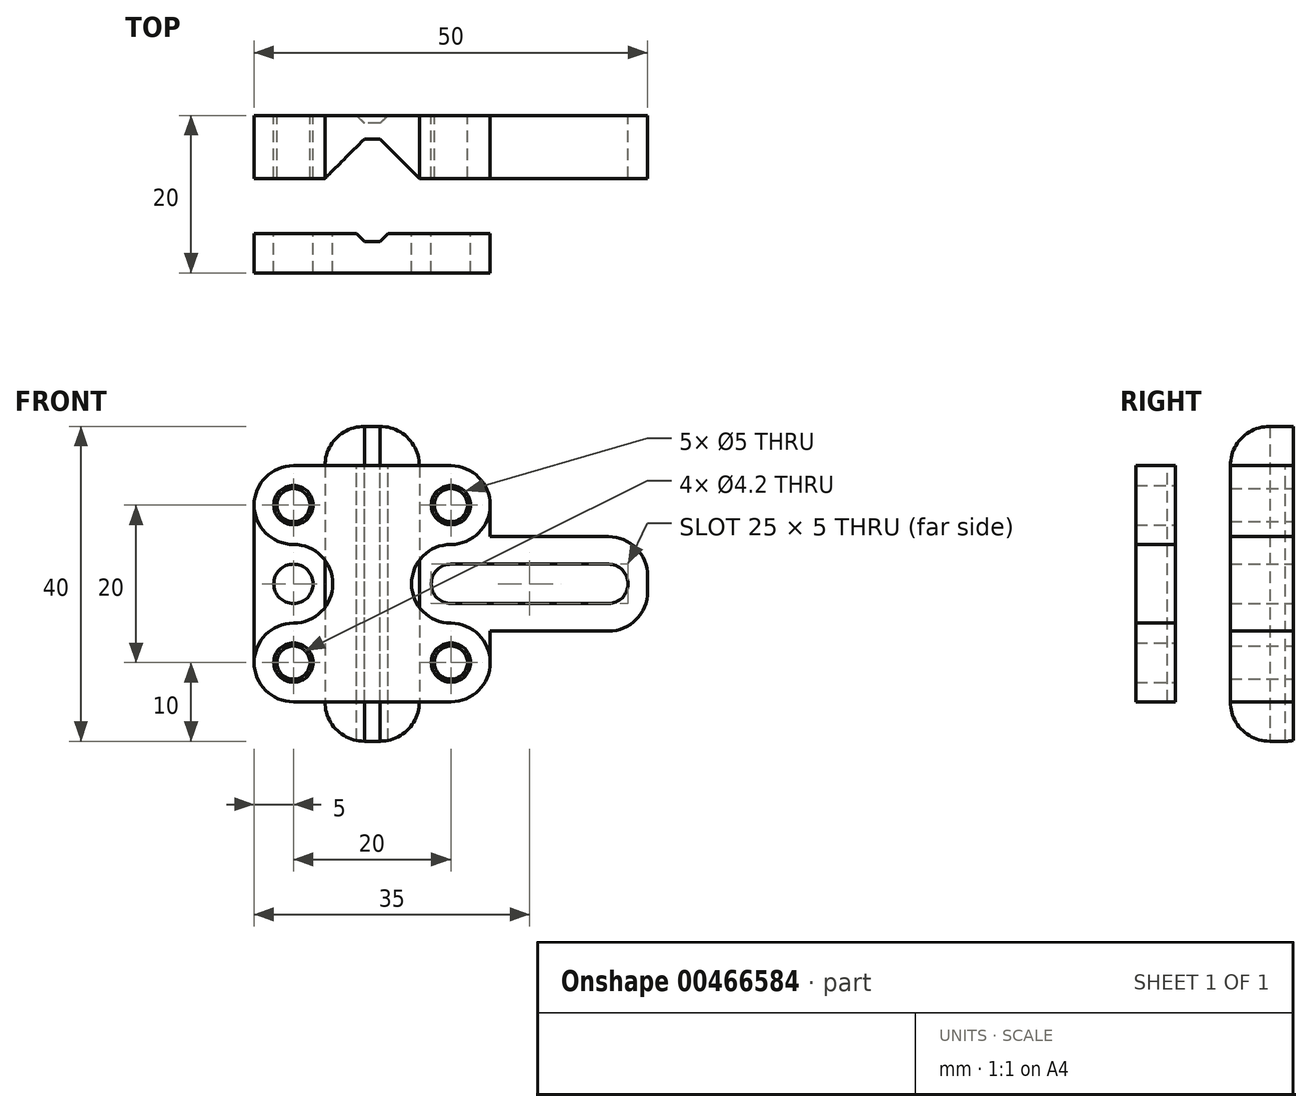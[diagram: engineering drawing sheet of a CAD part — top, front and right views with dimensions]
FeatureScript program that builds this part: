
annotation { "Feature Type Name" : "Feature", "Feature Type Description" : "" }
export const myFeature = defineFeature(function(context is Context, id is Id, definition is map)
    precondition{}
    {
        {
            var Q0;
            Q0=qCreatedBy(makeId("Front.planeOp"),FACE);
            var sketch = newSketch(context, id + "F0", { "sketchPlane" : qUnion([Q0])});
            skCircle(sketch, "E0", {"center": v(0, 0) * mm, "radius": 2.5 * mm, "construction": true});
            skCircle(sketch, "E1.0.1.0", {"center": v(0, 10) * mm, "radius": 2.5 * mm, "construction": true});
            skCircle(sketch, "E1.0.2.0", {"center": v(0, 20) * mm, "radius": 2.5 * mm, "construction": true});
            skCircle(sketch, "E1.0.3.0", {"center": v(0, 30) * mm, "radius": 2.5 * mm, "construction": true});
            skCircle(sketch, "E1.0.4.0", {"center": v(0, 40) * mm, "radius": 2.5 * mm, "construction": true});
            skCircle(sketch, "E1.1.0.0", {"center": v(10, 0) * mm, "radius": 2.5 * mm, "construction": true});
            skCircle(sketch, "E1.1.1.0", {"center": v(10, 10) * mm, "radius": 2.5 * mm, "construction": true});
            skCircle(sketch, "E1.1.2.0", {"center": v(10, 20) * mm, "radius": 2.5 * mm, "construction": true});
            skCircle(sketch, "E1.1.3.0", {"center": v(10, 30) * mm, "radius": 2.5 * mm, "construction": true});
            skCircle(sketch, "E1.1.4.0", {"center": v(10, 40) * mm, "radius": 2.5 * mm, "construction": true});
            skCircle(sketch, "E1.2.0.0", {"center": v(20, 0) * mm, "radius": 2.5 * mm, "construction": true});
            skCircle(sketch, "E1.2.1.0", {"center": v(20, 10) * mm, "radius": 2.1 * mm, "construction": true});
            skCircle(sketch, "E1.2.2.0", {"center": v(20, 20) * mm, "radius": 2.5 * mm});
            skCircle(sketch, "E1.2.3.0", {"center": v(20, 30) * mm, "radius": 2.1 * mm, "construction": true});
            skCircle(sketch, "E1.2.4.0", {"center": v(20, 40) * mm, "radius": 2.5 * mm, "construction": true});
            skCircle(sketch, "E1.3.0.0", {"center": v(30, 0) * mm, "radius": 2.5 * mm, "construction": true});
            skCircle(sketch, "E1.3.1.0", {"center": v(30, 10) * mm, "radius": 2.5 * mm, "construction": true});
            skCircle(sketch, "E1.3.2.0", {"center": v(30, 20) * mm, "radius": 2.5 * mm, "construction": true});
            skCircle(sketch, "E1.3.3.0", {"center": v(30, 30) * mm, "radius": 2.5 * mm, "construction": true});
            skCircle(sketch, "E1.3.4.0", {"center": v(30, 40) * mm, "radius": 2.5 * mm, "construction": true});
            skCircle(sketch, "E1.4.0.0", {"center": v(40, 0) * mm, "radius": 2.5 * mm, "construction": true});
            skCircle(sketch, "E1.4.1.0", {"center": v(40, 10) * mm, "radius": 2.1 * mm, "construction": true});
            skArc(sketch, "E1.4.2.0", {"start": v(40, 22.5) * mm, "mid": v(37.5, 20) * mm, "end": v(40, 17.5) * mm});
            skCircle(sketch, "E1.4.3.0", {"center": v(40, 30) * mm, "radius": 2.1 * mm, "construction": true});
            skCircle(sketch, "E1.4.4.0", {"center": v(40, 40) * mm, "radius": 2.5 * mm, "construction": true});
            skCircle(sketch, "E1.5.0.0", {"center": v(50, 0) * mm, "radius": 2.5 * mm, "construction": true});
            skCircle(sketch, "E1.5.1.0", {"center": v(50, 10) * mm, "radius": 2.5 * mm, "construction": true});
            skCircle(sketch, "E1.5.3.0", {"center": v(50, 30) * mm, "radius": 2.5 * mm, "construction": true});
            skCircle(sketch, "E1.5.4.0", {"center": v(50, 40) * mm, "radius": 2.5 * mm, "construction": true});
            skCircle(sketch, "E1.6.0.0", {"center": v(60, 0) * mm, "radius": 2.5 * mm, "construction": true});
            skCircle(sketch, "E1.6.1.0", {"center": v(60, 10) * mm, "radius": 2.5 * mm, "construction": true});
            skArc(sketch, "E1.6.2.0", {"start": v(60, 17.5) * mm, "mid": v(62.5, 20) * mm, "end": v(60, 22.5) * mm});
            skCircle(sketch, "E1.6.3.0", {"center": v(60, 30) * mm, "radius": 2.5 * mm, "construction": true});
            skCircle(sketch, "E1.6.4.0", {"center": v(60, 40) * mm, "radius": 2.5 * mm, "construction": true});
            skCircle(sketch, "E1.7.0.0", {"center": v(70, 0) * mm, "radius": 2.5 * mm, "construction": true});
            skCircle(sketch, "E1.7.1.0", {"center": v(70, 10) * mm, "radius": 2.5 * mm, "construction": true});
            skCircle(sketch, "E1.7.2.0", {"center": v(70, 20) * mm, "radius": 2.5 * mm, "construction": true});
            skCircle(sketch, "E1.7.3.0", {"center": v(70, 30) * mm, "radius": 2.5 * mm, "construction": true});
            skCircle(sketch, "E1.7.4.0", {"center": v(70, 40) * mm, "radius": 2.5 * mm, "construction": true});
            skCircle(sketch, "E1.8.0.0", {"center": v(80, 0) * mm, "radius": 2.5 * mm, "construction": true});
            skCircle(sketch, "E1.8.1.0", {"center": v(80, 10) * mm, "radius": 2.5 * mm, "construction": true});
            skCircle(sketch, "E1.8.2.0", {"center": v(80, 20) * mm, "radius": 2.5 * mm, "construction": true});
            skCircle(sketch, "E1.8.3.0", {"center": v(80, 30) * mm, "radius": 2.5 * mm, "construction": true});
            skCircle(sketch, "E1.8.4.0", {"center": v(80, 40) * mm, "radius": 2.5 * mm, "construction": true});
            skLineSegment(sketch, "E1.direction1", {"start": v(0, 0) * mm, "end": v(10, 0) * mm, "construction": true});
            skLineSegment(sketch, "E1.direction2", {"start": v(0, 0) * mm, "end": v(0, 10) * mm, "construction": true});
            skLineSegment(sketch, "E2.bottom", {"start": v(36, 0) * mm, "end": v(24, 0) * mm});
            skLineSegment(sketch, "E2.top", {"start": v(36, 40) * mm, "end": v(24, 40) * mm});
            skLineSegment(sketch, "E2.left", {"start": v(36, 0) * mm, "end": v(36, 5) * mm});
            skLineSegment(sketch, "E2.right", {"start": v(24, 0) * mm, "end": v(24, 5) * mm});
            skLineSegment(sketch, "E3.bottom", {"start": v(65, 14) * mm, "end": v(45, 14) * mm});
            skLineSegment(sketch, "E3.top", {"start": v(65, 26) * mm, "end": v(45, 26) * mm});
            skLineSegment(sketch, "E3.left", {"start": v(65, 14) * mm, "end": v(65, 26) * mm});
            skLineSegment(sketch, "E3.right", {"start": v(15, 14) * mm, "end": v(15, 26) * mm});
            skLineSegment(sketch, "E4.trimOffspring", {"start": v(24, 35) * mm, "end": v(24, 40) * mm});
            skLineSegment(sketch, "E5.trimOffspring", {"start": v(36, 35) * mm, "end": v(36, 40) * mm});
            skLineSegment(sketch, "E6", {"start": v(40, 22.5) * mm, "end": v(60, 22.5) * mm});
            skLineSegment(sketch, "E7", {"start": v(60, 17.5) * mm, "end": v(40, 17.5) * mm});
            skLineSegment(sketch, "E8", {"start": v(15, 26) * mm, "end": v(15, 35) * mm});
            skLineSegment(sketch, "E9", {"start": v(15, 35) * mm, "end": v(24, 35) * mm});
            skLineSegment(sketch, "E10", {"start": v(45, 35) * mm, "end": v(45, 26) * mm});
            skLineSegment(sketch, "E11", {"start": v(45, 5) * mm, "end": v(36, 5) * mm});
            skLineSegment(sketch, "E12", {"start": v(15, 5) * mm, "end": v(15, 14) * mm});
            skLineSegment(sketch, "E13.trimOffspring", {"start": v(36, 35) * mm, "end": v(45, 35) * mm});
            skLineSegment(sketch, "E14.trimOffspring", {"start": v(24, 5) * mm, "end": v(15, 5) * mm});
            skLineSegment(sketch, "E15.trimOffspring", {"start": v(45, 14) * mm, "end": v(45, 5) * mm});
            skSolve(sketch);
        }
        {
            var Q0;
            Q0=makeQuery(id+"F0.imprint","IMPRINT",FACE,{"disambiguationData":[TD([[makeQuery(id+"F0.imprint","IMPRINT",EDGE,{"derivedFrom":sQuery(id+"F0.wireOp",EDGE,"E1.2.1.0")}),-1.0]])]});
            var Q1;
            Q1=makeQuery(id+"F0.imprint","IMPRINT",FACE,{"disambiguationData":[TD([[makeQuery(id+"F0.imprint","IMPRINT",EDGE,{"derivedFrom":sQuery(id+"F0.wireOp",EDGE,"E1.2.2.0")}),-1.0]])]});
            extrude(context, id + "F1", {"entities" : qUnion([Q0, Q1]), "depth" : 8 * mm});
        }
        {
            var Q0;
            Q0=qCreatedBy(makeId("Top.planeOp"),FACE);
            var sketch = newSketch(context, id + "F2", { "sketchPlane" : qUnion([Q0])});
            skLineSegment(sketch, "E16", {"start": v(24, -8) * mm, "end": v(29, -3) * mm});
            skLineSegment(sketch, "E17", {"start": v(29, -3) * mm, "end": v(31, -3) * mm});
            skLineSegment(sketch, "E18", {"start": v(31, -3) * mm, "end": v(36, -8) * mm});
            skLineSegment(sketch, "E19", {"start": v(36, -8) * mm, "end": v(24, -8) * mm});
            skSolve(sketch);
        }
        {
            var Q0;
            Q0=makeQuery(id+"F2.imprint","IMPRINT",FACE,{"disambiguationData":[TD([[makeQuery(id+"F2.imprint","IMPRINT",EDGE,{"derivedFrom":sQuery(id+"F2.wireOp",EDGE,"E16")}),-1.0]])]});
            extrude(context, id + "F3", {"entities" : qUnion([Q0]), "operationType" : NewBodyOperationType.REMOVE, "depth" : 40 * mm});
        }
        {
            var Q0;
            Q0=sQuery(id+"F0.wireOp",VERTEX,"E1.2.3.0.center");
            var Q1;
            Q1=sQuery(id+"F0.wireOp",VERTEX,"E1.4.3.0.center");
            var Q2;
            Q2=sQuery(id+"F0.wireOp",VERTEX,"E1.4.1.0.center");
            var Q3;
            Q3=sQuery(id+"F0.wireOp",VERTEX,"E1.2.1.0.center");
            var Q4;
            Q4=makeQuery(id+"F1.opExtrude","SWEPT_BODY",BODY,{"disambiguationData":[OSD([sQuery(id+"F0.wireOp",EDGE,"E1.2.1.0"),sQuery(id+"F0.wireOp",EDGE,"E1.2.2.0"),sQuery(id+"F0.wireOp",EDGE,"E1.2.3.0"),sQuery(id+"F0.wireOp",EDGE,"E1.4.1.0"),sQuery(id+"F0.wireOp",EDGE,"E1.4.2.0"),sQuery(id+"F0.wireOp",EDGE,"E1.4.3.0"),sQuery(id+"F0.wireOp",EDGE,"E1.6.2.0"),sQuery(id+"F0.wireOp",EDGE,"E2.bottom"),sQuery(id+"F0.wireOp",EDGE,"E2.top"),sQuery(id+"F0.wireOp",EDGE,"E2.left"),sQuery(id+"F0.wireOp",EDGE,"E2.right"),sQuery(id+"F0.wireOp",EDGE,"E3.bottom"),sQuery(id+"F0.wireOp",EDGE,"E3.top"),sQuery(id+"F0.wireOp",EDGE,"E3.left"),sQuery(id+"F0.wireOp",EDGE,"E3.right"),sQuery(id+"F0.wireOp",EDGE,"E4.trimOffspring"),sQuery(id+"F0.wireOp",EDGE,"E5.trimOffspring"),sQuery(id+"F0.wireOp",EDGE,"E6"),sQuery(id+"F0.wireOp",EDGE,"E7"),sQuery(id+"F0.wireOp",EDGE,"E8"),sQuery(id+"F0.wireOp",EDGE,"E9"),sQuery(id+"F0.wireOp",EDGE,"E10"),sQuery(id+"F0.wireOp",EDGE,"E11"),sQuery(id+"F0.wireOp",EDGE,"E12"),sQuery(id+"F0.wireOp",EDGE,"E13.trimOffspring"),sQuery(id+"F0.wireOp",EDGE,"E14.trimOffspring"),sQuery(id+"F0.wireOp",EDGE,"E15.trimOffspring")])]});
            hole(context, id + "F4", {"style" : HoleStyle.SIMPLE, "endStyle" : HoleEndStyle.THROUGH, "oppositeDirection" : true, "standardTappedOrClearance" : lookupTablePath({ "standard" : "ISO", "engagement" : "75%", "pitch" : "0.8 mm", "size" : "M5", "type" : "Tapped" }), "standardBlindInLast" : lookupTablePath({ "standard" : "ISO", "engagement" : "75%", "pitch" : "0.8 mm", "size" : "M5", "type" : "Tapped" }), "holeDiameter" : 4.2 * mm, "showTappedDepth" : true, "isTappedThrough" : true, "tappedDepth" : 12 * mm, "tapClearance" : 3, "locations" : qUnion([Q0, Q1, Q2, Q3]), "scope" : qUnion([Q4]), "majorDiameter" : 5 * mm});
        }
        {
            var Q0;
            Q0=makeQuery(id+"F1.opExtrude","SWEPT_EDGE",EDGE,{"disambiguationData":[OSD([sQuery(id+"F0.wireOp",EDGE,"E2.top"),sQuery(id+"F0.wireOp",EDGE,"E5.trimOffspring")])]});
            var Q1;
            Q1=makeQuery(id+"F1.opExtrude","SWEPT_EDGE",EDGE,{"disambiguationData":[OSD([sQuery(id+"F0.wireOp",EDGE,"E2.top"),sQuery(id+"F0.wireOp",EDGE,"E4.trimOffspring")])]});
            var Q2;
            Q2=makeQuery(id+"F1.opExtrude","SWEPT_EDGE",EDGE,{"disambiguationData":[OSD([sQuery(id+"F0.wireOp",EDGE,"E10"),sQuery(id+"F0.wireOp",EDGE,"E13.trimOffspring")])]});
            var Q3;
            Q3=makeQuery(id+"F1.opExtrude","SWEPT_EDGE",EDGE,{"disambiguationData":[OSD([sQuery(id+"F0.wireOp",EDGE,"E8"),sQuery(id+"F0.wireOp",EDGE,"E9")])]});
            var Q4;
            Q4=makeQuery(id+"F1.opExtrude","SWEPT_EDGE",EDGE,{"disambiguationData":[OSD([sQuery(id+"F0.wireOp",EDGE,"E12"),sQuery(id+"F0.wireOp",EDGE,"E14.trimOffspring")])]});
            var Q5;
            Q5=makeQuery(id+"F1.opExtrude","SWEPT_EDGE",EDGE,{"disambiguationData":[OSD([sQuery(id+"F0.wireOp",EDGE,"E2.bottom"),sQuery(id+"F0.wireOp",EDGE,"E2.left")])]});
            var Q6;
            Q6=makeQuery(id+"F1.opExtrude","SWEPT_EDGE",EDGE,{"disambiguationData":[OSD([sQuery(id+"F0.wireOp",EDGE,"E2.bottom"),sQuery(id+"F0.wireOp",EDGE,"E2.right")])]});
            var Q7;
            Q7=makeQuery(id+"F1.opExtrude","SWEPT_EDGE",EDGE,{"disambiguationData":[OSD([sQuery(id+"F0.wireOp",EDGE,"E11"),sQuery(id+"F0.wireOp",EDGE,"E15.trimOffspring")])]});
            var Q8;
            Q8=makeQuery(id+"F1.opExtrude","SWEPT_EDGE",EDGE,{"disambiguationData":[OSD([sQuery(id+"F0.wireOp",EDGE,"E3.top"),sQuery(id+"F0.wireOp",EDGE,"E3.left")])]});
            var Q9;
            Q9=makeQuery(id+"F1.opExtrude","SWEPT_EDGE",EDGE,{"disambiguationData":[OSD([sQuery(id+"F0.wireOp",EDGE,"E3.bottom"),sQuery(id+"F0.wireOp",EDGE,"E3.left")])]});
            fillet(context, id + "F5", {"entities" : qUnion([Q0, Q1, Q2, Q3, Q4, Q5, Q6, Q7, Q8, Q9]), "radius" : 5 * mm, "tangentPropagation" : true, "allowEdgeOverflow" : false});
        }
        {
            var Q0;
            Q0=qCreatedBy(makeId("Front.planeOp"),FACE);
            var sketch = newSketch(context, id + "F6", { "sketchPlane" : qUnion([Q0])});
            skLineSegment(sketch, "E20.bottom", {"start": v(45, 35) * mm, "end": v(15, 35) * mm});
            skLineSegment(sketch, "E20.top", {"start": v(45, 5) * mm, "end": v(15, 5) * mm});
            skLineSegment(sketch, "E20.left", {"start": v(45, 35) * mm, "end": v(45, 5) * mm});
            skLineSegment(sketch, "E20.right", {"start": v(15, 35) * mm, "end": v(15, 5) * mm});
            skPoint(sketch, "E20.middle", {"position": v(30, 20) * mm});
            skArc(sketch, "E21", {"start": v(40, 25) * mm, "mid": v(35, 20) * mm, "end": v(40, 15) * mm});
            skArc(sketch, "E22", {"start": v(20, 15) * mm, "mid": v(25, 20) * mm, "end": v(20, 25) * mm});
            skLineSegment(sketch, "E23", {"start": v(40, 25) * mm, "end": v(45, 25) * mm});
            skLineSegment(sketch, "E24", {"start": v(40, 15) * mm, "end": v(45, 15) * mm});
            skLineSegment(sketch, "E25", {"start": v(20, 25) * mm, "end": v(15, 25) * mm});
            skLineSegment(sketch, "E26", {"start": v(20, 15) * mm, "end": v(15, 15) * mm});
            skSolve(sketch);
        }
        {
            var Q0;
            {var subQ4=sQuery(id+"F6.wireOp",EDGE,"E20.bottom");Q0=makeQuery(id+"F6.imprint","IMPRINT",FACE,{"disambiguationData":[TD([[makeQuery(id+"F6.imprint","IMPRINT",EDGE,{"derivedFrom":subQ4}),1.0]])]});}
            extrude(context, id + "F7", {"entities" : qUnion([Q0]), "depth" : 5 * mm});
        }
        {
            var Q0;
            Q0=sQuery(id+"F0.wireOp",VERTEX,"E1.4.3.0.center");
            var Q1;
            Q1=sQuery(id+"F0.wireOp",VERTEX,"E1.2.3.0.center");
            var Q2;
            Q2=sQuery(id+"F0.wireOp",VERTEX,"E1.2.1.0.center");
            var Q3;
            Q3=sQuery(id+"F0.wireOp",VERTEX,"E1.4.1.0.center");
            var Q4;
            Q4=makeQuery(id+"F7.opExtrude","SWEPT_BODY",BODY,{"disambiguationData":[OSD([sQuery(id+"F6.wireOp",EDGE,"E20.bottom"),sQuery(id+"F6.wireOp",EDGE,"E20.top"),sQuery(id+"F6.wireOp",EDGE,"E20.left"),sQuery(id+"F6.wireOp",EDGE,"E20.right")])]});
            hole(context, id + "F8", {"style" : HoleStyle.SIMPLE, "endStyle" : HoleEndStyle.THROUGH, "oppositeDirection" : true, "holeDiameter" : 5 * mm, "isTappedThrough" : true, "tappedDepth" : 12 * mm, "tapClearance" : 3, "locations" : qUnion([Q0, Q1, Q2, Q3]), "scope" : qUnion([Q4])});
        }
        {
            var Q0;
            Q0=makeQuery(id+"F7.opExtrude","SWEPT_EDGE",EDGE,{"disambiguationData":[OSD([sQuery(id+"F6.wireOp",EDGE,"E20.bottom"),sQuery(id+"F6.wireOp",EDGE,"E20.left")])]});
            var Q1;
            Q1=makeQuery(id+"F7.opExtrude","SWEPT_EDGE",EDGE,{"disambiguationData":[OSD([sQuery(id+"F6.wireOp",EDGE,"E20.bottom"),sQuery(id+"F6.wireOp",EDGE,"E20.right")])]});
            var Q2;
            Q2=makeQuery(id+"F7.opExtrude","SWEPT_EDGE",EDGE,{"disambiguationData":[OSD([sQuery(id+"F6.wireOp",EDGE,"E20.top"),sQuery(id+"F6.wireOp",EDGE,"E20.left")])]});
            var Q3;
            Q3=makeQuery(id+"F7.opExtrude","SWEPT_EDGE",EDGE,{"disambiguationData":[OSD([sQuery(id+"F6.wireOp",EDGE,"E20.top"),sQuery(id+"F6.wireOp",EDGE,"E20.right")])]});
            fillet(context, id + "F9", {"entities" : qUnion([Q0, Q1, Q2, Q3]), "radius" : 5 * mm, "tangentPropagation" : true, "allowEdgeOverflow" : false});
        }
        {
            var Q0;
            Q0=makeQuery(id+"F7.opExtrude","SWEPT_FACE",FACE,{"disambiguationData":[OSD([sQuery(id+"F6.wireOp",EDGE,"E20.bottom")])]});
            var sketch = newSketch(context, id + "F10", { "sketchPlane" : qUnion([Q0])});
            skPoint(sketch, "E27.endSnap0", {"position": v(30, 0) * mm});
            skLineSegment(sketch, "E28", {"start": v(28, 0) * mm, "end": v(32, 0) * mm});
            skPoint(sketch, "E29.orphan", {"position": v(30, 2) * mm});
            skPoint(sketch, "E30.orphan", {"position": v(30, -2.5) * mm});
            skLineSegment(sketch, "E31.MirrorCS", {"start": v(29, -1) * mm, "end": v(31, -1) * mm});
            skLineSegment(sketch, "E32.MirrorCS", {"start": v(32, 0) * mm, "end": v(31, -1) * mm});
            skLineSegment(sketch, "E33.MirrorCS", {"start": v(29, -1) * mm, "end": v(28, 0) * mm});
            skPoint(sketch, "E27.end.orphan", {"position": v(31, 1) * mm});
            skPoint(sketch, "E34.start.orphan", {"position": v(29, 1) * mm});
            skSolve(sketch);
        }
        {
            var Q0;
            Q0=qSketchRegion(id+"F10",true);
            var Q1;
            Q1=qConstructionFilter(qBodyType(qCreatedBy(id+"F10",EDGE),BodyType.WIRE),ConstructionObject.NO);
            extrude(context, id + "F11", {"entities" : qUnion([Q0]), "operationType" : NewBodyOperationType.REMOVE, "surfaceEntities" : qUnion([Q1]), "oppositeDirection" : true, "depth" : 50 * mm});
        }
        {
            var Q0;
            Q0=makeQuery(id+"F7.opExtrude","SWEPT_BODY",BODY,{"disambiguationData":[OSD([sQuery(id+"F6.wireOp",EDGE,"E20.bottom"),sQuery(id+"F6.wireOp",EDGE,"E20.top"),sQuery(id+"F6.wireOp",EDGE,"E20.left"),sQuery(id+"F6.wireOp",EDGE,"E20.right")])]});
            transform(context, id + "F12", {"entities" : qUnion([Q0]), "transformType" : TransformType.TRANSLATION_3D, "dx" : 0 * mm, "dy" : -15 * mm, "dz" : 0 * mm, "makeCopy" : false});
        }
        {
            var Q0;
            Q0=makeQuery(id+"F7.opExtrude","SWEPT_EDGE",EDGE,{"disambiguationData":[OSD([sQuery(id+"F6.wireOp",EDGE,"E20.right"),sQuery(id+"F6.wireOp",EDGE,"E25")])]});
            var Q1;
            Q1=makeQuery(id+"F7.opExtrude","SWEPT_EDGE",EDGE,{"disambiguationData":[OSD([sQuery(id+"F6.wireOp",EDGE,"E20.left"),sQuery(id+"F6.wireOp",EDGE,"E23")])]});
            var Q2;
            Q2=makeQuery(id+"F7.opExtrude","SWEPT_EDGE",EDGE,{"disambiguationData":[OSD([sQuery(id+"F6.wireOp",EDGE,"E20.left"),sQuery(id+"F6.wireOp",EDGE,"E24")])]});
            var Q3;
            Q3=makeQuery(id+"F7.opExtrude","SWEPT_EDGE",EDGE,{"disambiguationData":[OSD([sQuery(id+"F6.wireOp",EDGE,"E20.right"),sQuery(id+"F6.wireOp",EDGE,"E26")])]});
            fillet(context, id + "F13", {"entities" : qUnion([Q0, Q1, Q2, Q3]), "radius" : 5 * mm, "tangentPropagation" : true, "allowEdgeOverflow" : false});
        }
    });
